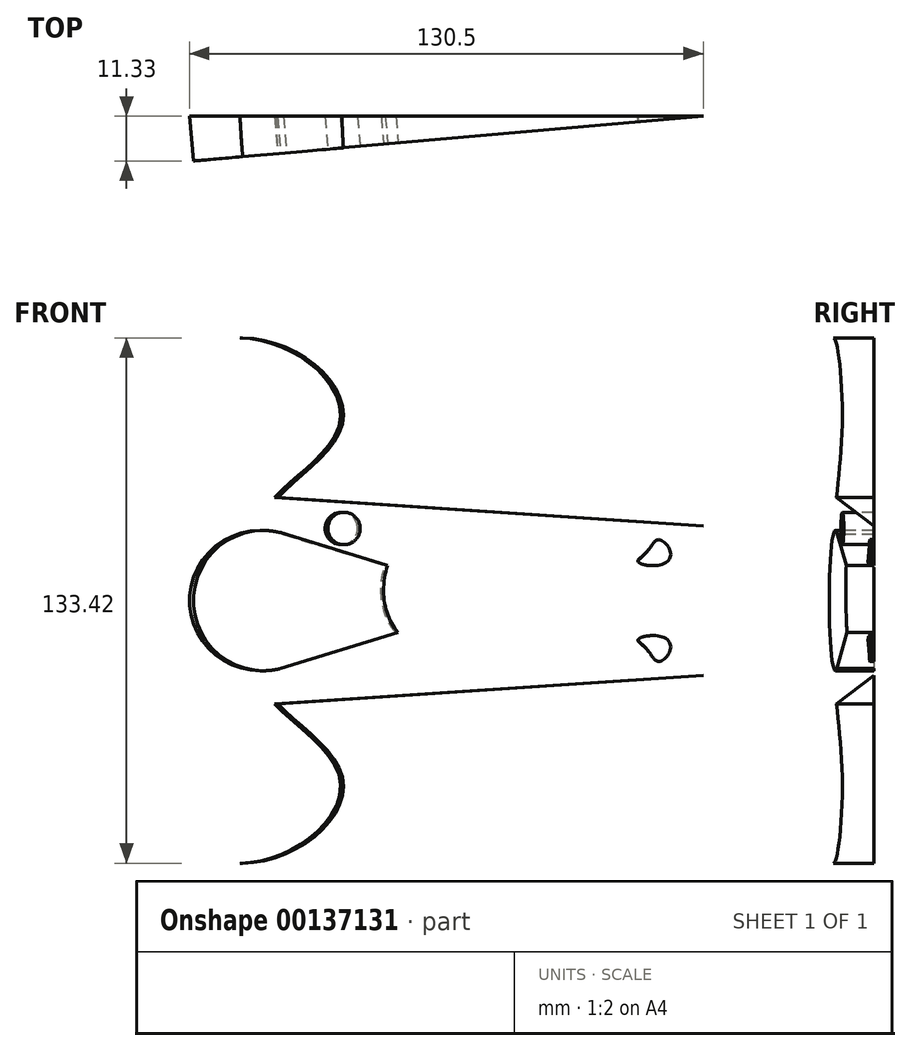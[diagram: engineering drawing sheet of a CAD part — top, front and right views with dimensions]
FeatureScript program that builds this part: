
annotation { "Feature Type Name" : "Feature", "Feature Type Description" : "" }
export const myFeature = defineFeature(function(context is Context, id is Id, definition is map)
    precondition{}
    {
        {
            var Q0;
            Q0=qCreatedBy(makeId("Front.planeOp"),FACE);
            var sketch = newSketch(context, id + "F0", { "sketchPlane" : qUnion([Q0])});
            skLineSegment(sketch, "E0", {"start": v(-75.22, 0) * mm, "end": v(39.78, 0) * mm});
            skCircle(sketch, "E1", {"center": v(-75.22, 0) * mm, "radius": 27 * mm});
            skLineSegment(sketch, "E2", {"start": v(-68.7, -26.2) * mm, "end": v(39.78, -19) * mm});
            skLineSegment(sketch, "E3.MirrorCS", {"start": v(-68.7, 26.2) * mm, "end": v(39.78, 19) * mm});
            skFitSpline(sketch, "E4", {"points": [v(-68.7, 26.2) * mm, v(-52.5, 43.92) * mm, v(-59.16, 59.8) * mm, v(-80.93, 66.46) * mm, v(-95.52, 55.96) * mm, v(-97.83, 36.75) * mm, v(-76.32, 20.1) * mm, v(-68.7, 26.2) * mm]});
            skFitSpline(sketch, "E5.MirrorC", {"points": [v(-68.7, -26.2) * mm, v(-52.5, -43.92) * mm, v(-59.16, -59.8) * mm, v(-80.93, -66.46) * mm, v(-95.52, -55.96) * mm, v(-97.83, -36.75) * mm, v(-76.32, -20.1) * mm, v(-68.7, -26.2) * mm]});
            skLineSegment(sketch, "E6", {"start": v(39.78, -19) * mm, "end": v(39.78, 19) * mm});
            skSolve(sketch);
        }
        {
            var Q0;
            {var subQ0=sQuery(id+"F0.wireOp",EDGE,"E4");var subQ1=sQuery(id+"F0.wireOp",EDGE,"E1");var subQ3=makeQuery(id+"F0.imprint","INTERSECT",VERTEX,{"derivedFrom":[subQ1,subQ0]});Q0=makeQuery(id+"F0.imprint","IMPRINT",FACE,{"disambiguationData":[TD([[makeQuery(id+"F0.imprint","IMPRINT",EDGE,{"disambiguationData":[TD([[subQ3,1.0]])],"derivedFrom":subQ1}),-1.0]])]});}
            var Q1;
            {var subQ0=sQuery(id+"F0.wireOp",EDGE,"E4");var subQ1=sQuery(id+"F0.wireOp",EDGE,"E1");var subQ3=makeQuery(id+"F0.imprint","INTERSECT",VERTEX,{"derivedFrom":[subQ1,subQ0]});Q1=makeQuery(id+"F0.imprint","IMPRINT",FACE,{"disambiguationData":[TD([[makeQuery(id+"F0.imprint","IMPRINT",EDGE,{"disambiguationData":[TD([[subQ3,1.0]])],"derivedFrom":subQ1}),1.0]])]});}
            var Q2;
            {var subQ0=sQuery(id+"F0.wireOp",EDGE,"E4");var subQ1=sQuery(id+"F0.wireOp",EDGE,"E1");var subQ3=makeQuery(id+"F0.imprint","INTERSECT",VERTEX,{"derivedFrom":[subQ1,subQ0]});Q2=makeQuery(id+"F0.imprint","IMPRINT",FACE,{"disambiguationData":[TD([[makeQuery(id+"F0.imprint","IMPRINT",EDGE,{"disambiguationData":[TD([[subQ3,-1.0]])],"derivedFrom":subQ1}),1.0]])]});}
            var Q3;
            {var subQ0=sQuery(id+"F0.wireOp",EDGE,"E5.MirrorC");var subQ1=sQuery(id+"F0.wireOp",EDGE,"E1");var subQ3=makeQuery(id+"F0.imprint","INTERSECT",VERTEX,{"derivedFrom":[subQ1,subQ0]});Q3=makeQuery(id+"F0.imprint","IMPRINT",FACE,{"disambiguationData":[TD([[makeQuery(id+"F0.imprint","IMPRINT",EDGE,{"disambiguationData":[TD([[subQ3,-1.0]])],"derivedFrom":subQ1}),1.0]])]});}
            var Q4;
            {var subQ0=sQuery(id+"F0.wireOp",EDGE,"E5.MirrorC");var subQ1=sQuery(id+"F0.wireOp",EDGE,"E1");var subQ3=makeQuery(id+"F0.imprint","INTERSECT",VERTEX,{"derivedFrom":[subQ1,subQ0]});Q4=makeQuery(id+"F0.imprint","IMPRINT",FACE,{"disambiguationData":[TD([[makeQuery(id+"F0.imprint","IMPRINT",EDGE,{"disambiguationData":[TD([[subQ3,-1.0]])],"derivedFrom":subQ1}),-1.0]])]});}
            var Q5;
            {var subQ5=sQuery(id+"F0.wireOp",EDGE,"E2");Q5=makeQuery(id+"F0.imprint","IMPRINT",FACE,{"disambiguationData":[TD([[makeQuery(id+"F0.imprint","IMPRINT",EDGE,{"derivedFrom":subQ5}),1.0]])]});}
            var Q6;
            {var subQ5=sQuery(id+"F0.wireOp",EDGE,"E3.MirrorCS");Q6=makeQuery(id+"F0.imprint","IMPRINT",FACE,{"disambiguationData":[TD([[makeQuery(id+"F0.imprint","IMPRINT",EDGE,{"derivedFrom":subQ5}),-1.0]])]});}
            var Q7;
            Q7=sQuery(id+"F0.wireOp",EDGE,"E6");
            revolve(context, id + "F1", {"entities" : qUnion([Q0, Q1, Q2, Q3, Q4, Q5, Q6]), "axis" : qUnion([Q7]), "revolveType" : RevolveType.ONE_DIRECTION, "angle" : 5 * degree});
        }
        {
            var Q0;
            Q0=makeQuery(id+"F1.opRevolve","CAP_FACE",FACE,{"disambiguationData":[OSD([sQuery(id+"F0.wireOp",EDGE,"E1"),sQuery(id+"F0.wireOp",EDGE,"E2"),sQuery(id+"F0.wireOp",EDGE,"E3.MirrorCS"),sQuery(id+"F0.wireOp",EDGE,"E4"),sQuery(id+"F0.wireOp",EDGE,"E5.MirrorC"),sQuery(id+"F0.wireOp",EDGE,"E6")])],"isStart":false});
            var sketch = newSketch(context, id + "F2", { "sketchPlane" : qUnion([Q0])});
            skCircle(sketch, "E7", {"center": v(-72.56, 0) * mm, "radius": 17.82 * mm});
            skLineSegment(sketch, "E8", {"start": v(-68.14, -17.26) * mm, "end": v(-11.64, 0) * mm});
            skLineSegment(sketch, "E9.MirrorCS", {"start": v(-68.14, 17.26) * mm, "end": v(-11.64, 0) * mm});
            skLineSegment(sketch, "E10.bottom", {"start": v(23.07, 12.16) * mm, "end": v(11.24, 12.16) * mm});
            skLineSegment(sketch, "E10.top", {"start": v(23.07, -12.16) * mm, "end": v(11.24, -12.16) * mm});
            skLineSegment(sketch, "E10.left", {"start": v(23.07, 12.16) * mm, "end": v(23.07, -12.16) * mm});
            skLineSegment(sketch, "E10.right", {"start": v(11.24, 12.16) * mm, "end": v(11.24, -12.16) * mm});
            skPoint(sketch, "E10.middle", {"position": v(17.16, 0) * mm});
            skFitSpline(sketch, "E11", {"points": [v(25.13, 12.16) * mm, v(28.21, 15.49) * mm, v(31.3, 12.16) * mm, v(28.73, 9.09) * mm, v(23.07, 9.86) * mm, v(25.13, 12.16) * mm]});
            skFitSpline(sketch, "E12.MirrorC", {"points": [v(25.13, -12.16) * mm, v(28.21, -15.49) * mm, v(31.3, -12.16) * mm, v(28.73, -9.09) * mm, v(23.07, -9.86) * mm, v(25.13, -12.16) * mm]});
            skFitSpline(sketch, "E13", {"points": [v(11.24, -12.16) * mm, v(-5.98, -14.22) * mm, v(-32.46, -12.16) * mm, v(-41.71, 0) * mm, v(-36.06, 15.23) * mm, v(-10.35, 14.46) * mm, v(11.24, 12.16) * mm, v(17.16, 6.53) * mm, v(11.24, -12.16) * mm]});
            skCircle(sketch, "E14", {"center": v(-52, -18.32) * mm, "radius": 4.11 * mm});
            skCircle(sketch, "E15.MirrorC", {"center": v(-52, 18.32) * mm, "radius": 4.11 * mm});
            skSolve(sketch);
        }
        {
            var Q0;
            {var subQ0=sQuery(id+"F2.wireOp",EDGE,"E8");var subQ1=sQuery(id+"F2.wireOp",EDGE,"E7");var subQ2=makeQuery(id+"F2.imprint","INTERSECT",VERTEX,{"disambiguationData":[OD(0.0)],"derivedFrom":[subQ1,subQ0]});Q0=makeQuery(id+"F2.imprint","IMPRINT",FACE,{"disambiguationData":[TD([[makeQuery(id+"F2.imprint","IMPRINT",EDGE,{"disambiguationData":[TD([[subQ2,1.0]])],"derivedFrom":subQ1}),1.0]])]});}
            var Q1;
            {var subQ0=sQuery(id+"F2.wireOp",EDGE,"E9.MirrorCS");var subQ1=sQuery(id+"F2.wireOp",EDGE,"E7");var subQ2=makeQuery(id+"F2.imprint","INTERSECT",VERTEX,{"disambiguationData":[OD(1.0)],"derivedFrom":[subQ1,subQ0]});Q1=makeQuery(id+"F2.imprint","IMPRINT",FACE,{"disambiguationData":[TD([[makeQuery(id+"F2.imprint","IMPRINT",EDGE,{"disambiguationData":[TD([[subQ2,1.0]])],"derivedFrom":subQ1}),-1.0]])]});}
            var Q2;
            {var subQ0=sQuery(id+"F2.wireOp",EDGE,"E9.MirrorCS");var subQ1=sQuery(id+"F2.wireOp",EDGE,"E8");var subQ2=makeQuery(id+"F2.imprint","INTERSECT",VERTEX,{"derivedFrom":[subQ1,subQ0]});Q2=makeQuery(id+"F2.imprint","IMPRINT",FACE,{"disambiguationData":[TD([[makeQuery(id+"F2.imprint","IMPRINT",EDGE,{"disambiguationData":[TD([[subQ2,1.0]])],"derivedFrom":subQ1}),1.0]])]});}
            var Q3;
            {var subQ0=sQuery(id+"F2.wireOp",EDGE,"E10.right");Q3=makeQuery(id+"F2.imprint","IMPRINT",FACE,{"disambiguationData":[TD([[makeQuery(id+"F2.imprint","IMPRINT",EDGE,{"derivedFrom":subQ0}),-1.0]])]});}
            var Q4;
            {var subQ6=sQuery(id+"F2.wireOp",EDGE,"E10.bottom");Q4=makeQuery(id+"F2.imprint","IMPRINT",FACE,{"disambiguationData":[TD([[makeQuery(id+"F2.imprint","IMPRINT",EDGE,{"derivedFrom":subQ6}),1.0]])]});}
            var Q5;
            {var subQ0=sQuery(id+"F2.wireOp",EDGE,"E10.right");Q5=makeQuery(id+"F2.imprint","IMPRINT",FACE,{"disambiguationData":[TD([[makeQuery(id+"F2.imprint","IMPRINT",EDGE,{"derivedFrom":subQ0}),1.0]])]});}
            var Q6;
            {var subQ0=sQuery(id+"F2.wireOp",EDGE,"E12.MirrorC");var subQ1=sQuery(id+"F2.wireOp",EDGE,"E10.left");var subQ2=makeQuery(id+"F2.imprint","INTERSECT",VERTEX,{"disambiguationData":[OD(0.0)],"derivedFrom":[subQ1,subQ0]});Q6=makeQuery(id+"F2.imprint","IMPRINT",FACE,{"disambiguationData":[TD([[makeQuery(id+"F2.imprint","IMPRINT",EDGE,{"disambiguationData":[TD([[subQ2,-1.0]])],"derivedFrom":subQ1}),1.0]])]});}
            var Q7;
            {var subQ0=sQuery(id+"F2.wireOp",EDGE,"E11");var subQ1=sQuery(id+"F2.wireOp",EDGE,"E10.left");var subQ2=makeQuery(id+"F2.imprint","INTERSECT",VERTEX,{"disambiguationData":[OD(0.0)],"derivedFrom":[subQ1,subQ0]});Q7=makeQuery(id+"F2.imprint","IMPRINT",FACE,{"disambiguationData":[TD([[makeQuery(id+"F2.imprint","IMPRINT",EDGE,{"disambiguationData":[TD([[subQ2,-1.0]])],"derivedFrom":subQ1}),1.0]])]});}
            var Q8;
            Q8=makeQuery(id+"F2.imprint","IMPRINT",FACE,{"disambiguationData":[TD([[makeQuery(id+"F2.imprint","IMPRINT",EDGE,{"derivedFrom":sQuery(id+"F2.wireOp",EDGE,"E14")}),1.0]])]});
            var Q9;
            Q9=makeQuery(id+"F2.imprint","IMPRINT",FACE,{"disambiguationData":[TD([[makeQuery(id+"F2.imprint","IMPRINT",EDGE,{"derivedFrom":sQuery(id+"F2.wireOp",EDGE,"E15.MirrorC")}),-1.0]])]});
            extrude(context, id + "F3", {"entities" : qUnion([Q0, Q1, Q2, Q3, Q4, Q5, Q6, Q7, Q8, Q9]), "operationType" : NewBodyOperationType.REMOVE, "oppositeDirection" : true, "depth" : 25 * mm});
        }
    });
